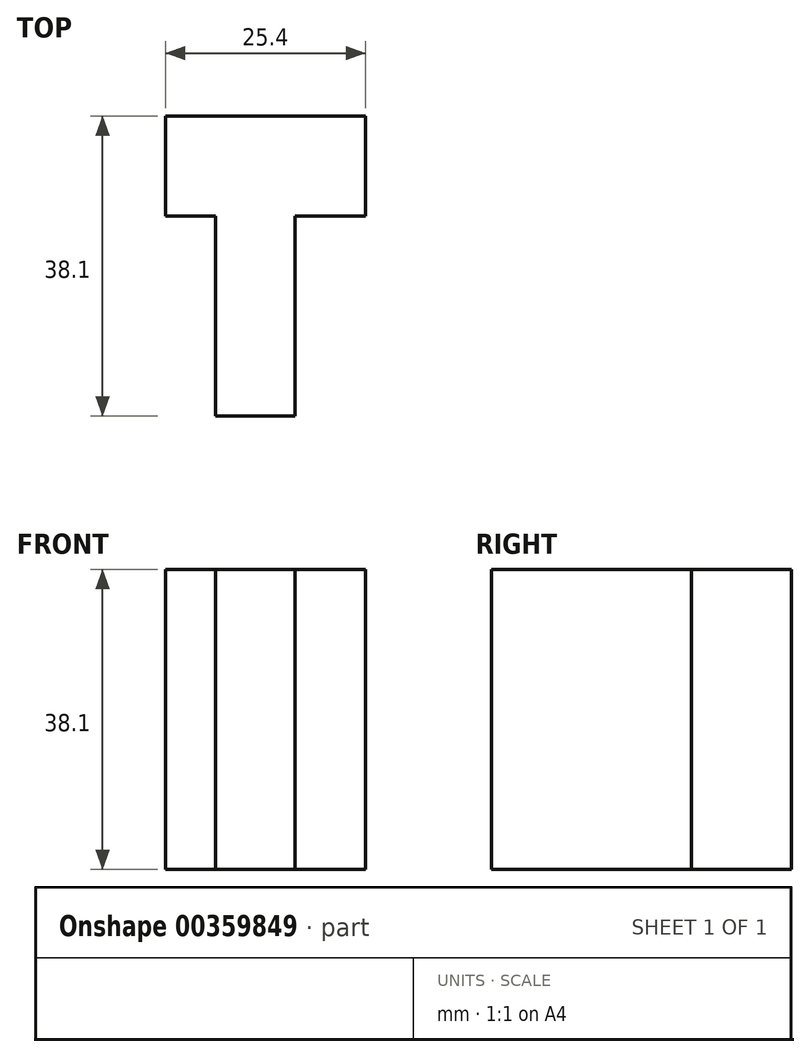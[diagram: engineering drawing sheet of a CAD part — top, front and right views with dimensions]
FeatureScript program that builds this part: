
annotation { "Feature Type Name" : "Feature", "Feature Type Description" : "" }
export const myFeature = defineFeature(function(context is Context, id is Id, definition is map)
    precondition{}
    {
        {
            var Q0;
            Q0=qCreatedBy(makeId("Top.planeOp"),FACE);
            var sketch = newSketch(context, id + "F0", { "sketchPlane" : qUnion([Q0])});
            skLineSegment(sketch, "E0", {"start": v(0, 0) * mm, "end": v(0, 25.4) * mm});
            skLineSegment(sketch, "E1", {"start": v(-6.35, 25.4) * mm, "end": v(-6.35, 38.1) * mm});
            skLineSegment(sketch, "E2", {"start": v(-6.35, 38.1) * mm, "end": v(19.05, 38.1) * mm});
            skLineSegment(sketch, "E3", {"start": v(19.05, 38.1) * mm, "end": v(19.05, 25.4) * mm});
            skLineSegment(sketch, "E4", {"start": v(19.05, 25.4) * mm, "end": v(10.12, 25.4) * mm});
            skLineSegment(sketch, "E5", {"start": v(10.12, 25.4) * mm, "end": v(10.12, 0) * mm});
            skLineSegment(sketch, "E6", {"start": v(10.12, 0) * mm, "end": v(-2.58, 0) * mm});
            skLineSegment(sketch, "E7", {"start": v(-2.58, 0) * mm, "end": v(0, 0) * mm});
            skLineSegment(sketch, "E8", {"start": v(-6.35, 25.4) * mm, "end": v(0, 25.4) * mm});
            skSolve(sketch);
        }
        {
            var Q0;
            Q0 = qSketchRegion(id + "F0", true);
            extrude(context, id + "F1", {"entities" : qUnion([Q0]), "depth" : 38.1 * mm});
        }
    });
